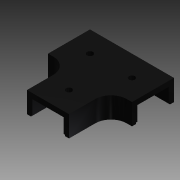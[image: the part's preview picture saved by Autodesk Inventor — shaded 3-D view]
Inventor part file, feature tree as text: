
AUTODESK INVENTOR PART (.ipt)
format: ipt  version: 2015 (Build 190159000, 159)  size: 158,720 bytes
history: native  units: in
note: dims shown in document units (in); Inventor stores cm internally (conversion verified against a paired STEP export)
features: extrude x6, sketch x6, other x3, split x1, fillet x1
ambient origin geometry x8: Origin, YZ Plane, XZ Plane, XY Plane, X Axis, Y Axis, Z Axis, Center Point
bodies: Solid1 (feature_tree)
feature tree (17):
  extrude  "Extrusion1"  Depth=1.0in
  extrude  "Extrusion2"  Depth=0.5in TaperAngle=0.0deg
  extrude  "Extrusion3"  Depth=0.75in
  extrude  "Extrusion4"  Depth=1.75in TaperAngle=0.0deg
  extrude  "Extrusion5"  Depth=0.75in
  split  "Split1"
  other  "Lip1"
  other  "Lip2"
  other  "Lip3"
  extrude  "Extrusion6"  Depth=0.375in
  fillet  "Fillet1"  Radius=1.0in
  sketch  "Sketch1"  dims[d0=1.0in d1=1.0in]
  sketch  "Sketch2"  dims[d2=2.0in d3=0.0in d4=0.5in d5=0.0in]
  sketch  "Sketch4"  dims[d6=0.5in d7=0.0in d8=0.75in]
  sketch  "Sketch5"  dims[d9=0.75in d10=1.75in d11=0.0in]
  sketch  "Sketch6"  dims[d12=0.75in d13=0.75in]
  sketch  "Sketch7"  dims[d14=1.75in d15=0.0in d16=0.03in d17=0.03in d18=0.0in d19=0.0in d20=0.0in d21=0.0in d22=0.03in d23=0.03in d24=0.0in d25=0.0in d26=0.0in d27=0.0in d28=0.03in d29=0.03in d30=0.0in d31=0.0in d32=0.0in d33=0.0in d34=0.141in d35=1.0in d36=0.0in d37=0.375in]
